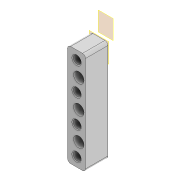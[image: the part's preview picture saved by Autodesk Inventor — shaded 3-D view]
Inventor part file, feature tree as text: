
AUTODESK INVENTOR PART (.ipt)
format: ipt  version: 2022 (Build 260153000, 153)  size: 194,560 bytes
history: native  units: mm
features: reference x12, other x6, sketch x3, plane x2, extrude x2, chamfer x2, hole x1, fillet x1, projected_geometry x1
ambient origin geometry x8: Origin, YZ Plane, XZ Plane, XY Plane, X Axis, Y Axis, Z Axis, Center Point
bodies: Volumenkörper1 (feature_tree)
feature tree (30):
  plane  "Arbeitsebene1"
  plane  "Arbeitsebene2"
  extrude  "Extrusion1"  Depth=8.0mm
  extrude  "Extrusion2"  Depth=8.0mm
  hole  "Bohrung1"  [1 undecoded]
  fillet  "Rundung1"  Radius=3.2mm
  chamfer  "Fase1"  Distance=3.2mm
  chamfer  "Fase2"  Distance=3.2mm
  sketch  "Skizze2"  dims[d0=8.0mm d1=8.0mm]
  reference  "Referenz1"
  reference  "Referenz2"
  reference  "Referenz3"
  reference  "Referenz4"
  reference  "Referenz5"
  reference  "Referenz6"
  reference  "Referenz7"
  reference  "Referenz8"
  reference  "Referenz9"
  reference  "Referenz10"
  reference  "Referenz11"
  reference  "Referenz12"
  sketch  "Skizze3"  dims[d2=8.0mm d3=8.0mm]
  projected_geometry  "Projizierte Kontur1"
  sketch  "Skizze4"  dims[d4=3.2mm d5=3.2mm d6=3.2mm d7=3.2mm d8=3.2mm d9=7.0mm d10=10.0mm d11=0.0mm d12=5.3mm d13=5.3mm d14=5.3mm d15=5.3mm d16=5.0mm d17=0.0mm d18=3.2mm d19=6.0mm d20=7.0mm d21=10.0mm d22=90.0deg d23=8.0mm d24=20.594885mm d25=2.0mm d26=0.5mm d27=2.0mm d28=45.0deg d29=1.3mm d30=2.0mm d31=45.0deg]
  other  "Omnicscope_Xiao.iam"
  other  "00_Seeeduino Xiao:1"
  other  "00_Seeeduino Xiao:7"
  other  "00_Seeeduino Xiao:13"
  other  "Omniscope_USBC_Bar:1"
  other  "00_Seeeduino Xiao:19"
note: 1 required parameter value undecoded (feature->parameter linkage not recoverable at this tier; creation-order binding heuristic only, values carry confidence <= 0.55)
